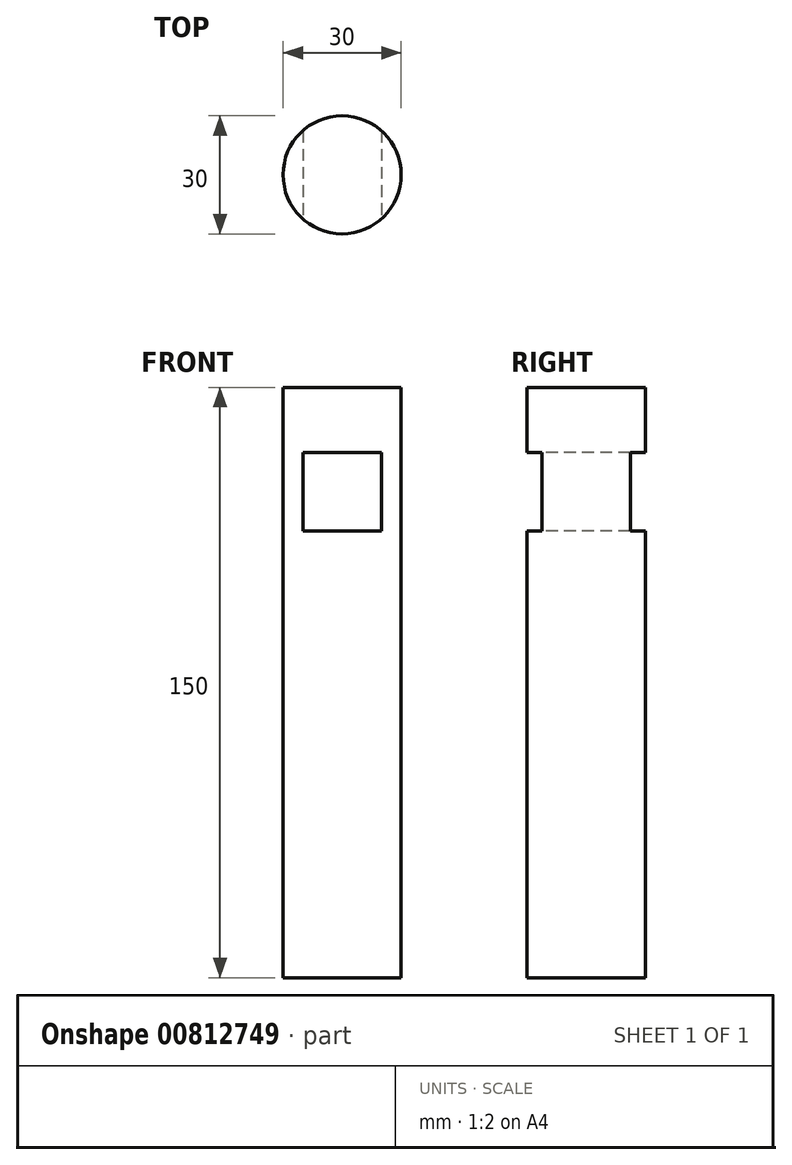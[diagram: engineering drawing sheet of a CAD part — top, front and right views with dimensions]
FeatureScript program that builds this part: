
annotation { "Feature Type Name" : "Feature", "Feature Type Description" : "" }
export const myFeature = defineFeature(function(context is Context, id is Id, definition is map)
    precondition{}
    {
        {
            var Q0;
            Q0=qCreatedBy(makeId("Top.planeOp"),FACE);
            var sketch = newSketch(context, id + "F0", { "sketchPlane" : qUnion([Q0])});
            skCircle(sketch, "E0", {"center": v(0, 0) * mm, "radius": 15 * mm});
            skSolve(sketch);
        }
        {
            var Q0;
            Q0=makeQuery(id+"F0.imprint","IMPRINT",FACE,{"disambiguationData":[TD([[makeQuery(id+"F0.imprint","IMPRINT",EDGE,{"derivedFrom":sQuery(id+"F0.wireOp",EDGE,"E0")}),1.0]])]});
            extrude(context, id + "F1", {"entities" : qUnion([Q0]), "depth" : 150 * mm, "offsetDistance" : 25 * mm});
        }
        {
            var Q0;
            Q0=qCreatedBy(makeId("Front.planeOp"),FACE);
            var sketch = newSketch(context, id + "F2", { "sketchPlane" : qUnion([Q0])});
            skLineSegment(sketch, "E1.bottom", {"start": v(-10, 133.47) * mm, "end": v(10, 133.47) * mm});
            skLineSegment(sketch, "E1.top", {"start": v(-10, 113.47) * mm, "end": v(10, 113.47) * mm});
            skLineSegment(sketch, "E1.left", {"start": v(-10, 133.47) * mm, "end": v(-10, 113.47) * mm});
            skLineSegment(sketch, "E1.right", {"start": v(10, 133.47) * mm, "end": v(10, 113.47) * mm});
            skSolve(sketch);
        }
        {
            var Q0;
            Q0 = qSketchRegion(id + "F2", true);
            extrude(context, id + "F3", {"entities" : qUnion([Q0]), "operationType" : NewBodyOperationType.REMOVE, "endBound" : BoundingType.SYMMETRIC, "oppositeDirection" : true, "depth" : 50 * mm, "offsetDistance" : 25 * mm});
        }
    });
